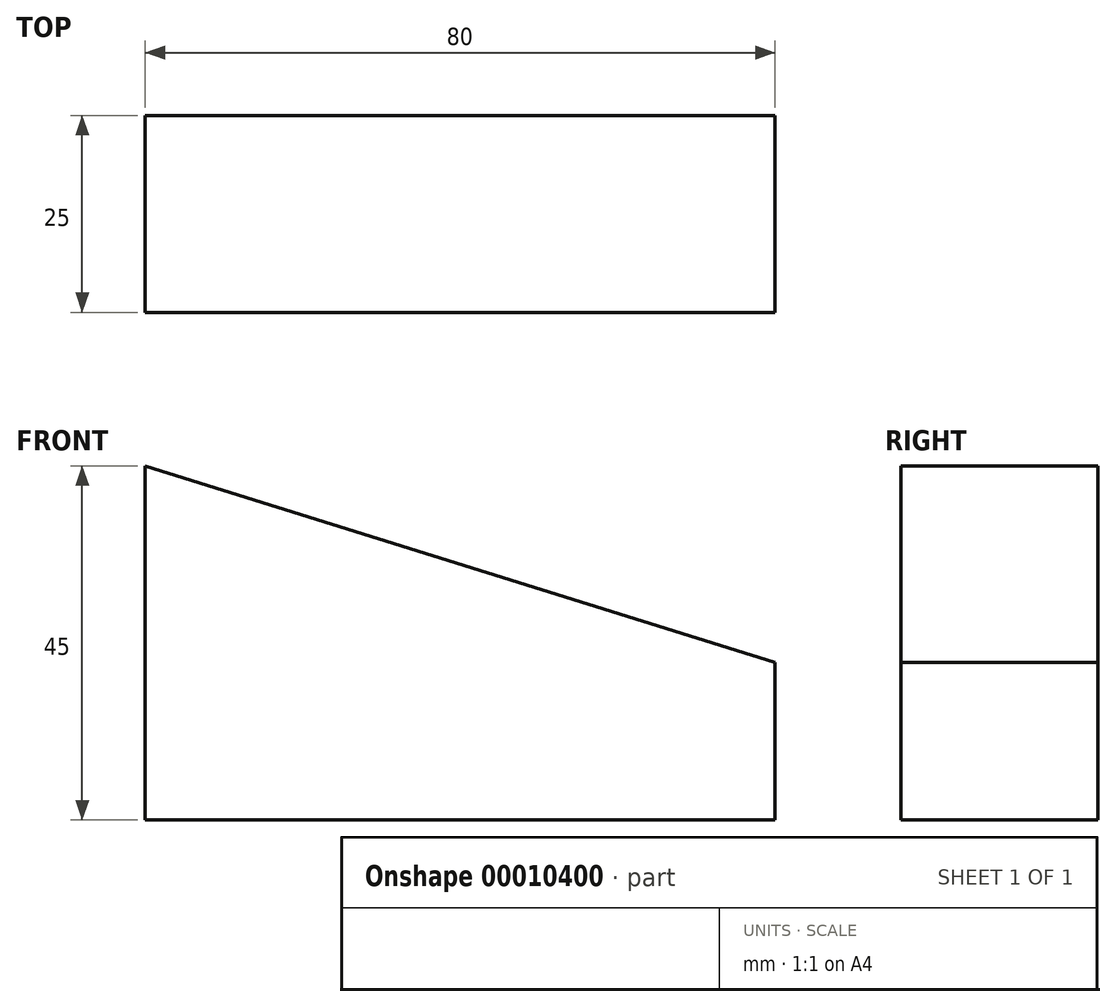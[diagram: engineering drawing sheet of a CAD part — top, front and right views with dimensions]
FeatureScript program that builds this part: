
annotation { "Feature Type Name" : "Feature", "Feature Type Description" : "" }
export const myFeature = defineFeature(function(context is Context, id is Id, definition is map)
    precondition{}
    {
        {
            var Q0;
            Q0=qCreatedBy(makeId("Front.planeOp"),FACE);
            var sketch = newSketch(context, id + "F0", { "sketchPlane" : qUnion([Q0])});
            skLineSegment(sketch, "E0", {"start": v(0, 0) * mm, "end": v(80, 0) * mm});
            skLineSegment(sketch, "E1", {"start": v(80, 0) * mm, "end": v(80, 20) * mm});
            skLineSegment(sketch, "E2", {"start": v(80, 20) * mm, "end": v(0, 45) * mm});
            skLineSegment(sketch, "E3", {"start": v(0, 45) * mm, "end": v(0, 0) * mm});
            skSolve(sketch);
        }
        {
            var Q0;
            Q0 = qSketchRegion(id + "F0", true);
            extrude(context, id + "F1", {"entities" : qUnion([Q0]), "oppositeDirection" : true, "depth" : 25 * mm});
        }
    });
